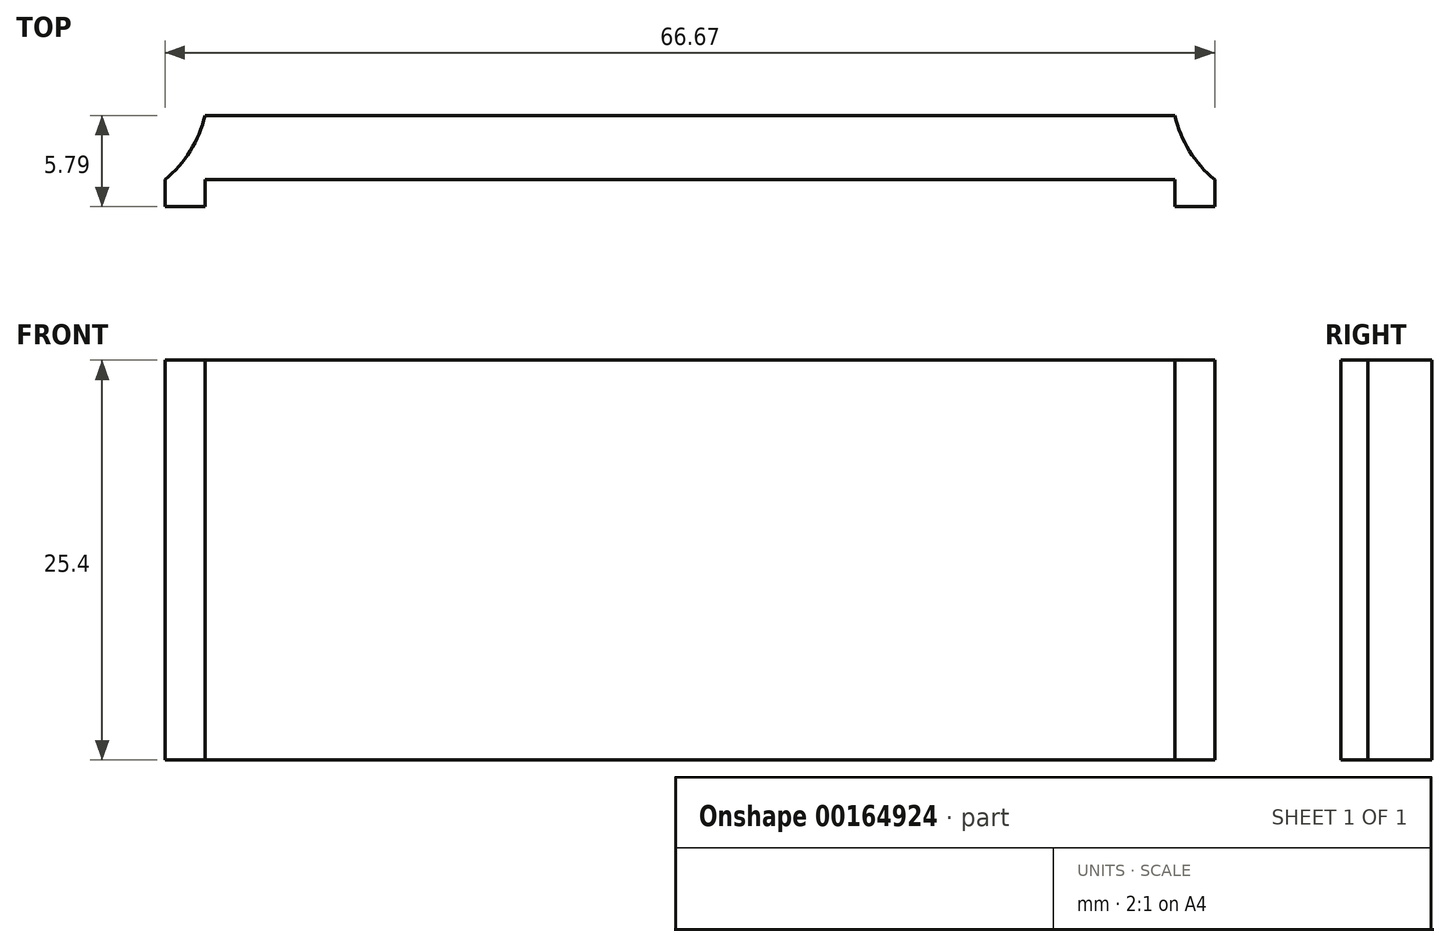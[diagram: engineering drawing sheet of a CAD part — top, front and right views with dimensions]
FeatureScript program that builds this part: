
annotation { "Feature Type Name" : "Feature", "Feature Type Description" : "" }
export const myFeature = defineFeature(function(context is Context, id is Id, definition is map)
    precondition{}
    {
        {
            var Q0;
            Q0=qCreatedBy(makeId("Top.planeOp"),FACE);
            var sketch = newSketch(context, id + "F0", { "sketchPlane" : qUnion([Q0])});
            skLineSegment(sketch, "E0", {"start": v(0, 0) * mm, "end": v(0, 1.7) * mm});
            skLineSegment(sketch, "E1", {"start": v(0, 0) * mm, "end": v(-4.77, 0) * mm, "construction": true});
            skArc(sketch, "E2", {"start": v(-4.77, 0) * mm, "mid": v(-2.23, 0.44) * mm, "end": v(0, 1.7) * mm, "construction": true});
            skArc(sketch, "E3", {"start": v(0, 1.7) * mm, "mid": v(1.6, 3.54) * mm, "end": v(2.54, 5.8) * mm});
            skLineSegment(sketch, "E4", {"start": v(-4.77, 7.5) * mm, "end": v(71.43, 7.5) * mm, "construction": true});
            skLineSegment(sketch, "E5", {"start": v(2.54, 5.8) * mm, "end": v(64.13, 5.8) * mm});
            skLineSegment(sketch, "E6", {"start": v(33.33, 7.5) * mm, "end": v(33.33, 5.8) * mm, "construction": true});
            skArc(sketch, "E7", {"start": v(64.13, 5.8) * mm, "mid": v(65.06, 3.54) * mm, "end": v(66.67, 1.7) * mm});
            skLineSegment(sketch, "E8", {"start": v(66.67, 0) * mm, "end": v(66.67, 1.7) * mm});
            skLineSegment(sketch, "E9", {"start": v(66.67, 0) * mm, "end": v(64.13, 0) * mm});
            skLineSegment(sketch, "E10", {"start": v(64.13, 0) * mm, "end": v(64.13, 1.7) * mm});
            skLineSegment(sketch, "E11", {"start": v(64.13, 1.7) * mm, "end": v(2.54, 1.7) * mm});
            skLineSegment(sketch, "E12", {"start": v(2.54, 1.7) * mm, "end": v(2.54, 0) * mm});
            skLineSegment(sketch, "E13", {"start": v(2.54, 0) * mm, "end": v(0, 0) * mm});
            skSolve(sketch);
        }
        {
            var Q0;
            Q0=qSketchRegion(id+"F0",true);
            extrude(context, id + "F1", {"entities" : qUnion([Q0]), "depth" : 25.4 * mm});
        }
    });
